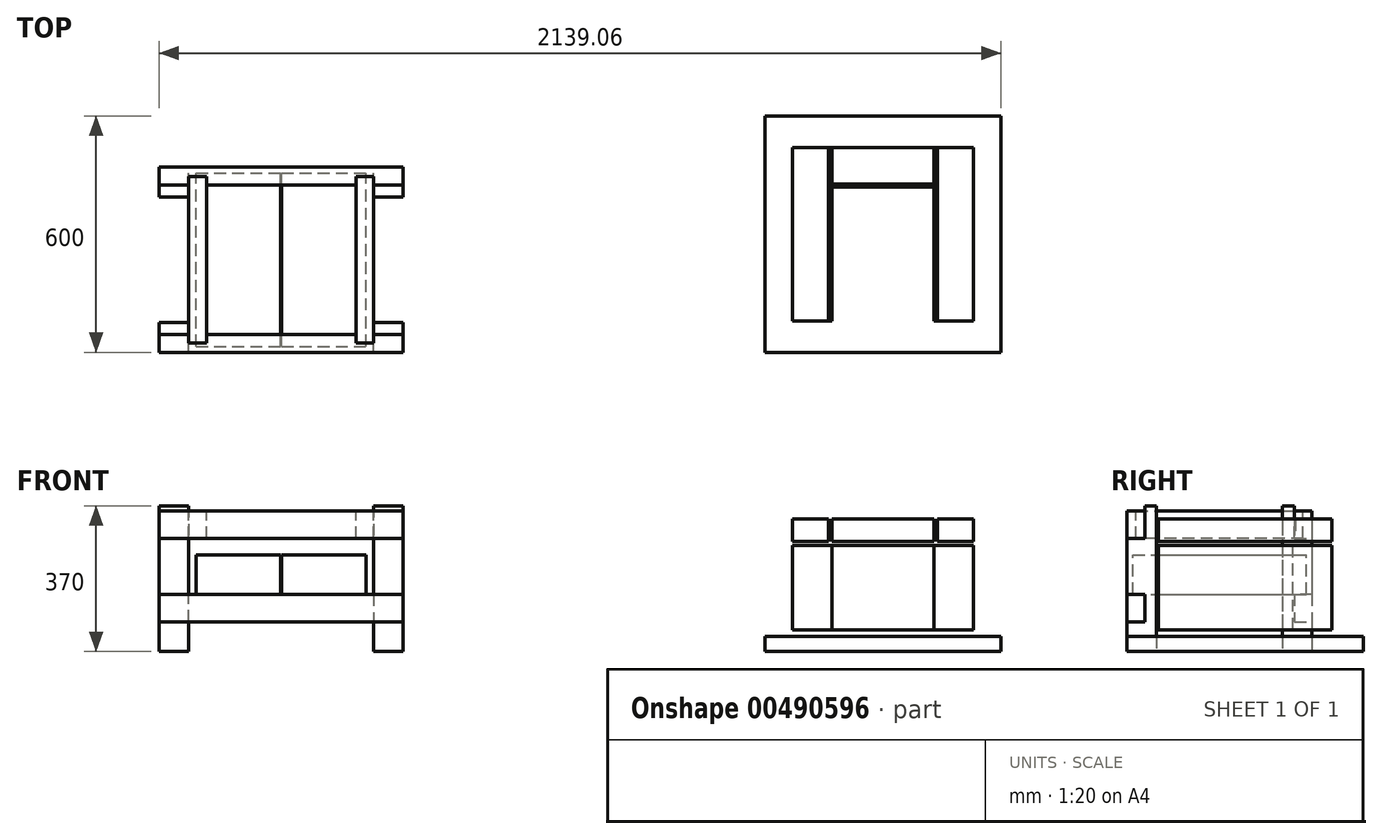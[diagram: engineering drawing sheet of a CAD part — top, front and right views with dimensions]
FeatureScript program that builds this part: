
annotation { "Feature Type Name" : "Feature", "Feature Type Description" : "" }
export const myFeature = defineFeature(function(context is Context, id is Id, definition is map)
    precondition{}
    {
        {
            var Q0;
            Q0=qCreatedBy(makeId("Top.planeOp"),FACE);
            var sketch = newSketch(context, id + "F0", { "sketchPlane" : qUnion([Q0])});
            skLineSegment(sketch, "E0.bottom", {"start": v(0, 470) * mm, "end": v(470, 470) * mm, "construction": true});
            skLineSegment(sketch, "E0.top", {"start": v(0, 0) * mm, "end": v(470, 0) * mm, "construction": true});
            skLineSegment(sketch, "E0.left", {"start": v(0, 470) * mm, "end": v(0, 0) * mm, "construction": true});
            skLineSegment(sketch, "E0.right", {"start": v(470, 470) * mm, "end": v(470, 0) * mm, "construction": true});
            skLineSegment(sketch, "E1.bottom", {"start": v(0, 0) * mm, "end": v(-75, 0) * mm});
            skLineSegment(sketch, "E1.top", {"start": v(0, 75) * mm, "end": v(-75, 75) * mm});
            skLineSegment(sketch, "E1.left", {"start": v(0, 0) * mm, "end": v(0, 75) * mm});
            skLineSegment(sketch, "E1.right", {"start": v(-75, 0) * mm, "end": v(-75, 75) * mm});
            skLineSegment(sketch, "E2.bottom", {"start": v(0, 470) * mm, "end": v(-75, 470) * mm});
            skLineSegment(sketch, "E2.top", {"start": v(0, 395) * mm, "end": v(-75, 395) * mm});
            skLineSegment(sketch, "E2.left", {"start": v(0, 470) * mm, "end": v(0, 395) * mm});
            skLineSegment(sketch, "E2.right", {"start": v(-75, 470) * mm, "end": v(-75, 395) * mm});
            skLineSegment(sketch, "E3.bottom", {"start": v(470, 470) * mm, "end": v(545, 470) * mm});
            skLineSegment(sketch, "E3.top", {"start": v(470, 395) * mm, "end": v(545, 395) * mm});
            skLineSegment(sketch, "E3.left", {"start": v(470, 470) * mm, "end": v(470, 395) * mm});
            skLineSegment(sketch, "E3.right", {"start": v(545, 470) * mm, "end": v(545, 395) * mm});
            skLineSegment(sketch, "E4.bottom", {"start": v(470, 0) * mm, "end": v(545, 0) * mm});
            skLineSegment(sketch, "E4.top", {"start": v(470, 75) * mm, "end": v(545, 75) * mm});
            skLineSegment(sketch, "E4.left", {"start": v(470, 0) * mm, "end": v(470, 75) * mm});
            skLineSegment(sketch, "E4.right", {"start": v(545, 0) * mm, "end": v(545, 75) * mm});
            skSolve(sketch);
        }
        {
            var Q0;
            Q0 = qSketchRegion(id + "F0", true);
            extrude(context, id + "F1", {"entities" : qUnion([Q0]), "depth" : 370 * mm, "offsetDistance" : 25 * mm});
        }
        {
            var Q0;
            Q0=makeQuery(id+"F1.opExtrude","SWEPT_FACE",FACE,{"disambiguationData":[OSD([sQuery(id+"F0.wireOp",EDGE,"E4.right")])]});
            var sketch = newSketch(context, id + "F2", { "sketchPlane" : qUnion([Q0])});
            skLineSegment(sketch, "E5", {"start": v(0, 491.28) * mm, "end": v(45, 491.28) * mm});
            skLineSegment(sketch, "E6", {"start": v(45, 491.28) * mm, "end": v(45, 287) * mm});
            skLineSegment(sketch, "E7", {"start": v(45, 287) * mm, "end": v(0, 287) * mm});
            skLineSegment(sketch, "E8", {"start": v(75, 370) * mm, "end": v(395, 370) * mm, "construction": true});
            skLineSegment(sketch, "E9", {"start": v(235, 370) * mm, "end": v(235, 0) * mm, "construction": true});
            skLineSegment(sketch, "E10", {"start": v(0, 491.28) * mm, "end": v(0, 287) * mm});
            skLineSegment(sketch, "E11.MirrorCS", {"start": v(425, 287) * mm, "end": v(470, 287) * mm});
            skLineSegment(sketch, "E12.MirrorCS", {"start": v(425, 491.28) * mm, "end": v(425, 287) * mm});
            skLineSegment(sketch, "E13.MirrorCS", {"start": v(470, 491.28) * mm, "end": v(470, 287) * mm});
            skLineSegment(sketch, "E14.MirrorCS", {"start": v(470, 491.28) * mm, "end": v(425, 491.28) * mm});
            skLineSegment(sketch, "E15", {"start": v(75, 0) * mm, "end": v(395, 0) * mm, "construction": true});
            skLineSegment(sketch, "E16", {"start": v(-8.8, 145) * mm, "end": v(45, 145) * mm});
            skLineSegment(sketch, "E17", {"start": v(45, 145) * mm, "end": v(45, 75) * mm});
            skLineSegment(sketch, "E18", {"start": v(45, 75) * mm, "end": v(-8.8, 75) * mm});
            skLineSegment(sketch, "E19", {"start": v(-8.8, 145) * mm, "end": v(-8.8, 75) * mm});
            skLineSegment(sketch, "E20.MirrorCS", {"start": v(478.8, 145) * mm, "end": v(478.8, 75) * mm});
            skLineSegment(sketch, "E21.MirrorCS", {"start": v(425, 75) * mm, "end": v(478.8, 75) * mm});
            skLineSegment(sketch, "E22.MirrorCS", {"start": v(478.8, 145) * mm, "end": v(425, 145) * mm});
            skLineSegment(sketch, "E23.MirrorCS", {"start": v(425, 145) * mm, "end": v(425, 75) * mm});
            skSolve(sketch);
        }
        {
            var Q0;
            Q0 = qSketchRegion(id + "F2", true);
            extrude(context, id + "F3", {"entities" : qUnion([Q0]), "operationType" : NewBodyOperationType.REMOVE, "endBound" : BoundingType.THROUGH_ALL, "oppositeDirection" : true, "depth" : 25 * mm, "offsetDistance" : 25 * mm});
        }
        {
            var Q0;
            Q0=makeQuery(id+"F1.opExtrude","SWEPT_FACE",FACE,{"disambiguationData":[OSD([sQuery(id+"F0.wireOp",EDGE,"E4.right")])]});
            var sketch = newSketch(context, id + "F4", { "sketchPlane" : qUnion([Q0])});
            skLineSegment(sketch, "E24.0", {"start": v(0, 357) * mm, "end": v(45, 357) * mm});
            skLineSegment(sketch, "E24.1", {"start": v(45, 357) * mm, "end": v(45, 287) * mm});
            skLineSegment(sketch, "E24.2", {"start": v(45, 287) * mm, "end": v(0, 287) * mm});
            skLineSegment(sketch, "E24.3", {"start": v(0, 145) * mm, "end": v(45, 145) * mm});
            skLineSegment(sketch, "E24.4", {"start": v(45, 145) * mm, "end": v(45, 75) * mm});
            skLineSegment(sketch, "E24.5", {"start": v(45, 75) * mm, "end": v(0, 75) * mm});
            skLineSegment(sketch, "E24.6", {"start": v(425, 75) * mm, "end": v(470, 75) * mm});
            skLineSegment(sketch, "E24.7", {"start": v(470, 145) * mm, "end": v(425, 145) * mm});
            skLineSegment(sketch, "E24.8", {"start": v(425, 145) * mm, "end": v(425, 75) * mm});
            skLineSegment(sketch, "E24.9", {"start": v(425, 287) * mm, "end": v(470, 287) * mm});
            skLineSegment(sketch, "E24.10", {"start": v(425, 357) * mm, "end": v(425, 287) * mm});
            skLineSegment(sketch, "E24.11", {"start": v(470, 357) * mm, "end": v(425, 357) * mm});
            skLineSegment(sketch, "E25", {"start": v(0, 357) * mm, "end": v(0, 287) * mm});
            skLineSegment(sketch, "E26", {"start": v(0, 145) * mm, "end": v(0, 75) * mm});
            skLineSegment(sketch, "E27", {"start": v(470, 145) * mm, "end": v(470, 75) * mm});
            skLineSegment(sketch, "E28", {"start": v(470, 357) * mm, "end": v(470, 287) * mm});
            skLineSegment(sketch, "E29.bottom", {"start": v(0, 295) * mm, "end": v(-22, 295) * mm, "construction": true});
            skLineSegment(sketch, "E29.top", {"start": v(0, 235) * mm, "end": v(-22, 235) * mm, "construction": true});
            skLineSegment(sketch, "E29.left", {"start": v(0, 295) * mm, "end": v(0, 235) * mm, "construction": true});
            skLineSegment(sketch, "E29.right", {"start": v(-22, 295) * mm, "end": v(-22, 235) * mm, "construction": true});
            skPoint(sketch, "E30.oppositeSnap0", {"position": v(-22, 265) * mm});
            skLineSegment(sketch, "E31", {"start": v(75, 370) * mm, "end": v(395, 0) * mm, "construction": true});
            skLineSegment(sketch, "E32", {"start": v(235, 185) * mm, "end": v(235, -27.84) * mm, "construction": true});
            skLineSegment(sketch, "E33.MirrorCS", {"start": v(470, 295) * mm, "end": v(492, 295) * mm, "construction": true});
            skPoint(sketch, "E34.MirrorP", {"position": v(492, 265) * mm});
            skLineSegment(sketch, "E35.MirrorCS", {"start": v(470, 295) * mm, "end": v(470, 235) * mm, "construction": true});
            skLineSegment(sketch, "E36.MirrorCS", {"start": v(470, 235) * mm, "end": v(492, 235) * mm, "construction": true});
            skLineSegment(sketch, "E37.MirrorCS", {"start": v(492, 295) * mm, "end": v(492, 235) * mm, "construction": true});
            skSolve(sketch);
        }
        {
            var Q0;
            Q0 = qSketchRegion(id + "F4", true);
            var Q1;
            Q1=makeQuery(id+"F1.opExtrude","SWEPT_FACE",FACE,{"disambiguationData":[OSD([sQuery(id+"F0.wireOp",EDGE,"E1.right")])]});
            extrude(context, id + "F5", {"entities" : qUnion([Q0]), "endBound" : BoundingType.UP_TO_SURFACE, "oppositeDirection" : true, "depth" : 25 * mm, "endBoundEntityFace" : qUnion([Q1]), "offsetDistance" : 25 * mm});
        }
        {
            var Q0;
            Q0=makeQuery(id+"F5.opExtrude","SWEPT_FACE",FACE,{"disambiguationData":[OSD([sQuery(id+"F4.wireOp",EDGE,"E24.0")])]});
            var sketch = newSketch(context, id + "F6", { "sketchPlane" : qUnion([Q0])});
            skLineSegment(sketch, "E38.0", {"start": v(470, 23) * mm, "end": v(470, 45) * mm});
            skLineSegment(sketch, "E39.0", {"start": v(425, 23) * mm, "end": v(425, 45) * mm});
            skLineSegment(sketch, "E40.0", {"start": v(425, 425) * mm, "end": v(470, 425) * mm});
            skLineSegment(sketch, "E41.trimOffspring", {"start": v(425, 425) * mm, "end": v(425, 447) * mm});
            skLineSegment(sketch, "E42.trimOffspring", {"start": v(470, 425) * mm, "end": v(470, 447) * mm});
            skLineSegment(sketch, "E43.0", {"start": v(425, 23) * mm, "end": v(470, 23) * mm});
            skLineSegment(sketch, "E44.0", {"start": v(425, 447) * mm, "end": v(470, 447) * mm});
            skLineSegment(sketch, "E45", {"start": v(235, 432.2) * mm, "end": v(235, 65.36) * mm, "construction": true});
            skPoint(sketch, "E45.startSnap0", {"position": v(235, 45) * mm});
            skLineSegment(sketch, "E46.MirrorCS", {"start": v(45, 425) * mm, "end": v(45, 447) * mm});
            skLineSegment(sketch, "E47.MirrorCS", {"start": v(0, 23) * mm, "end": v(0, 45) * mm});
            skLineSegment(sketch, "E48.MirrorCS", {"start": v(45, 23) * mm, "end": v(45, 45) * mm});
            skLineSegment(sketch, "E49.MirrorCS", {"start": v(0, 425) * mm, "end": v(0, 447) * mm});
            skLineSegment(sketch, "E50.MirrorCS", {"start": v(45, 447) * mm, "end": v(0, 447) * mm});
            skLineSegment(sketch, "E51.MirrorCS", {"start": v(45, 425) * mm, "end": v(0, 425) * mm});
            skLineSegment(sketch, "E52.MirrorCS", {"start": v(45, 23) * mm, "end": v(0, 23) * mm});
            skLineSegment(sketch, "E53.0", {"start": v(0, 45) * mm, "end": v(470, 45) * mm});
            skPoint(sketch, "E54.orphan", {"position": v(470, 37.95) * mm});
            skPoint(sketch, "E55.orphan", {"position": v(0, 37.95) * mm});
            skSolve(sketch);
        }
        {
            var Q0;
            Q0 = qSketchRegion(id + "F6", true);
            extrude(context, id + "F7", {"entities" : qUnion([Q0]), "operationType" : NewBodyOperationType.REMOVE, "oppositeDirection" : true, "depth" : 70 * mm, "offsetDistance" : 25 * mm});
        }
        {
            var Q0;
            Q0=makeQuery(id+"F5.opExtrude","SWEPT_FACE",FACE,{"disambiguationData":[OSD([sQuery(id+"F4.wireOp",EDGE,"E24.0")])]});
            var sketch = newSketch(context, id + "F8", { "sketchPlane" : qUnion([Q0])});
            skLineSegment(sketch, "E56.0", {"start": v(45, 23) * mm, "end": v(0, 23) * mm});
            skLineSegment(sketch, "E56.1", {"start": v(45, 447) * mm, "end": v(0, 447) * mm});
            skLineSegment(sketch, "E56.2", {"start": v(425, 447) * mm, "end": v(470, 447) * mm});
            skLineSegment(sketch, "E56.3", {"start": v(425, 23) * mm, "end": v(470, 23) * mm});
            skLineSegment(sketch, "E57", {"start": v(0, 23) * mm, "end": v(0, 447) * mm});
            skLineSegment(sketch, "E58", {"start": v(45, 447) * mm, "end": v(45, 23) * mm});
            skLineSegment(sketch, "E59", {"start": v(425, 23) * mm, "end": v(425, 447) * mm});
            skLineSegment(sketch, "E60", {"start": v(470, 23) * mm, "end": v(470, 447) * mm});
            skSolve(sketch);
        }
        {
            var Q0;
            Q0 = qSketchRegion(id + "F8", true);
            var Q1;
            Q1=makeQuery(id+"F5.opExtrude","SWEPT_FACE",FACE,{"disambiguationData":[OSD([sQuery(id+"F4.wireOp",EDGE,"E24.2")])]});
            extrude(context, id + "F9", {"entities" : qUnion([Q0]), "endBound" : BoundingType.UP_TO_SURFACE, "oppositeDirection" : true, "depth" : 25 * mm, "endBoundEntityFace" : qUnion([Q1]), "offsetDistance" : 25 * mm});
        }
        {
            var Q0;
            Q0=qCreatedBy(makeId("Front.planeOp"),FACE);
            cPlane(context, id + "F10", {"entities" : qUnion([Q0]), "cplaneType" : CPlaneType.OFFSET, "offset" : 235 * mm, "oppositeDirection" : true, "width" : 150 * mm, "height" : 150 * mm});
        }
        {
            var Q0;
            Q0=qCreatedBy(id+"F10.planeOp",FACE);
            var sketch = newSketch(context, id + "F11", { "sketchPlane" : qUnion([Q0])});
            skLineSegment(sketch, "E61.0", {"start": v(215, 163) * mm, "end": v(215, 145) * mm});
            skLineSegment(sketch, "E61.1", {"start": v(255, 145) * mm, "end": v(255, 127) * mm});
            skLineSegment(sketch, "E62.0", {"start": v(19, 145) * mm, "end": v(234, 145) * mm});
            skLineSegment(sketch, "E62.1", {"start": v(236, 145) * mm, "end": v(451, 145) * mm});
            skLineSegment(sketch, "E63", {"start": v(234, 145) * mm, "end": v(234, 245) * mm});
            skLineSegment(sketch, "E64", {"start": v(234, 245) * mm, "end": v(19, 245) * mm});
            skLineSegment(sketch, "E65", {"start": v(19, 245) * mm, "end": v(19, 145) * mm});
            skPoint(sketch, "E66.orphan", {"position": v(20, 145) * mm});
            skLineSegment(sketch, "E67", {"start": v(236, 145) * mm, "end": v(236, 245) * mm});
            skLineSegment(sketch, "E68", {"start": v(236, 245) * mm, "end": v(451, 245) * mm});
            skLineSegment(sketch, "E69", {"start": v(451, 245) * mm, "end": v(451, 145) * mm});
            skPoint(sketch, "E70.orphan", {"position": v(450, 145) * mm});
            skSolve(sketch);
        }
        {
            var Q0;
            Q0 = qSketchRegion(id + "F11", true);
            extrude(context, id + "F12", {"entities" : qUnion([Q0]), "depth" : 440 * mm, "offsetDistance" : 25 * mm, "symmetric" : true});
        }
        {
            var Q0;
            Q0=qCreatedBy(makeId("Top.planeOp"),FACE);
            var sketch = newSketch(context, id + "F13", { "sketchPlane" : qUnion([Q0])});
            skLineSegment(sketch, "E71.bottom", {"start": v(1464.06, 0) * mm, "end": v(2064.06, 0) * mm});
            skLineSegment(sketch, "E71.top", {"start": v(1464.06, 600) * mm, "end": v(2064.06, 600) * mm});
            skLineSegment(sketch, "E71.left", {"start": v(1464.06, 0) * mm, "end": v(1464.06, 600) * mm});
            skLineSegment(sketch, "E71.right", {"start": v(2064.06, 0) * mm, "end": v(2064.06, 600) * mm});
            skSolve(sketch);
        }
        {
            var Q0;
            Q0 = qSketchRegion(id + "F13", true);
            extrude(context, id + "F14", {"entities" : qUnion([Q0]), "depth" : 38 * mm, "offsetDistance" : 25 * mm});
        }
        {
            var Q0;
            Q0=qCreatedBy(makeId("Front.planeOp"),FACE);
            var sketch = newSketch(context, id + "F15", { "sketchPlane" : qUnion([Q0])});
            skLineSegment(sketch, "E72.0", {"start": v(1534.06, 54) * mm, "end": v(1634.06, 54) * mm});
            skLineSegment(sketch, "E73", {"start": v(1534.06, 54) * mm, "end": v(1534.06, 269) * mm});
            skLineSegment(sketch, "E74", {"start": v(1994.06, 54) * mm, "end": v(1994.06, 269) * mm});
            skLineSegment(sketch, "E75", {"start": v(1534.06, 269) * mm, "end": v(1634.06, 269) * mm});
            skLineSegment(sketch, "E76.0", {"start": v(1634.06, 54) * mm, "end": v(1634.06, 269) * mm});
            skLineSegment(sketch, "E77.0", {"start": v(1894.06, 54) * mm, "end": v(1894.06, 269) * mm});
            skLineSegment(sketch, "E78.trimOffspring", {"start": v(1894.06, 269) * mm, "end": v(1994.06, 269) * mm});
            skLineSegment(sketch, "E79.trimOffspring", {"start": v(1894.06, 54) * mm, "end": v(1994.06, 54) * mm});
            skLineSegment(sketch, "E80.0", {"start": v(1534.06, 279) * mm, "end": v(1564.06, 279) * mm});
            skLineSegment(sketch, "E81.0", {"start": v(1902.06, 279) * mm, "end": v(1994.06, 279) * mm});
            skLineSegment(sketch, "E82", {"start": v(1534.06, 279) * mm, "end": v(1534.06, 336) * mm});
            skLineSegment(sketch, "E83", {"start": v(1534.06, 336) * mm, "end": v(1626.06, 336) * mm});
            skLineSegment(sketch, "E84", {"start": v(1626.06, 336) * mm, "end": v(1626.06, 279) * mm});
            skLineSegment(sketch, "E85", {"start": v(1564.06, 279) * mm, "end": v(1626.06, 279) * mm});
            skLineSegment(sketch, "E86", {"start": v(1902.06, 336) * mm, "end": v(1994.06, 336) * mm});
            skLineSegment(sketch, "E87", {"start": v(1994.06, 336) * mm, "end": v(1994.06, 279) * mm});
            skLineSegment(sketch, "E88", {"start": v(1902.06, 336) * mm, "end": v(1902.06, 279) * mm});
            skSolve(sketch);
        }
        {
            var Q0;
            Q0 = qSketchRegion(id + "F15", true);
            extrude(context, id + "F16", {"entities" : qUnion([Q0]), "oppositeDirection" : true, "depth" : 520 * mm, "offsetDistance" : 25 * mm, "hasSecondDirection" : true, "secondDirectionOppositeDirection" : true, "secondDirectionDepth" : 80 * mm});
        }
        {
            var Q0;
            Q0=makeQuery(id+"F16.opExtrude","SWEPT_FACE",FACE,{"disambiguationData":[OSD([sQuery(id+"F15.wireOp",EDGE,"E76.0")])]});
            var sketch = newSketch(context, id + "F17", { "sketchPlane" : qUnion([Q0])});
            skLineSegment(sketch, "E89.0", {"start": v(520, 54) * mm, "end": v(520, 269) * mm});
            skLineSegment(sketch, "E89.1", {"start": v(520, 336) * mm, "end": v(520, 279) * mm});
            skLineSegment(sketch, "E90", {"start": v(520, 336) * mm, "end": v(428, 336) * mm});
            skLineSegment(sketch, "E91", {"start": v(428, 336) * mm, "end": v(428, 279) * mm});
            skLineSegment(sketch, "E92", {"start": v(428, 279) * mm, "end": v(520, 279) * mm});
            skLineSegment(sketch, "E93", {"start": v(520, 269) * mm, "end": v(420, 269) * mm});
            skLineSegment(sketch, "E94", {"start": v(420, 269) * mm, "end": v(420, 54) * mm});
            skLineSegment(sketch, "E95", {"start": v(420, 54) * mm, "end": v(520, 54) * mm});
            skSolve(sketch);
        }
        {
            var Q0;
            Q0 = qSketchRegion(id + "F17", true);
            var Q1;
            Q1=makeQuery(id+"F16.opExtrude","SWEPT_FACE",FACE,{"disambiguationData":[OSD([sQuery(id+"F15.wireOp",EDGE,"E77.0")])]});
            extrude(context, id + "F18", {"entities" : qUnion([Q0]), "endBound" : BoundingType.UP_TO_SURFACE, "depth" : 25 * mm, "endBoundEntityFace" : qUnion([Q1]), "offsetDistance" : 25 * mm});
        }
    });
